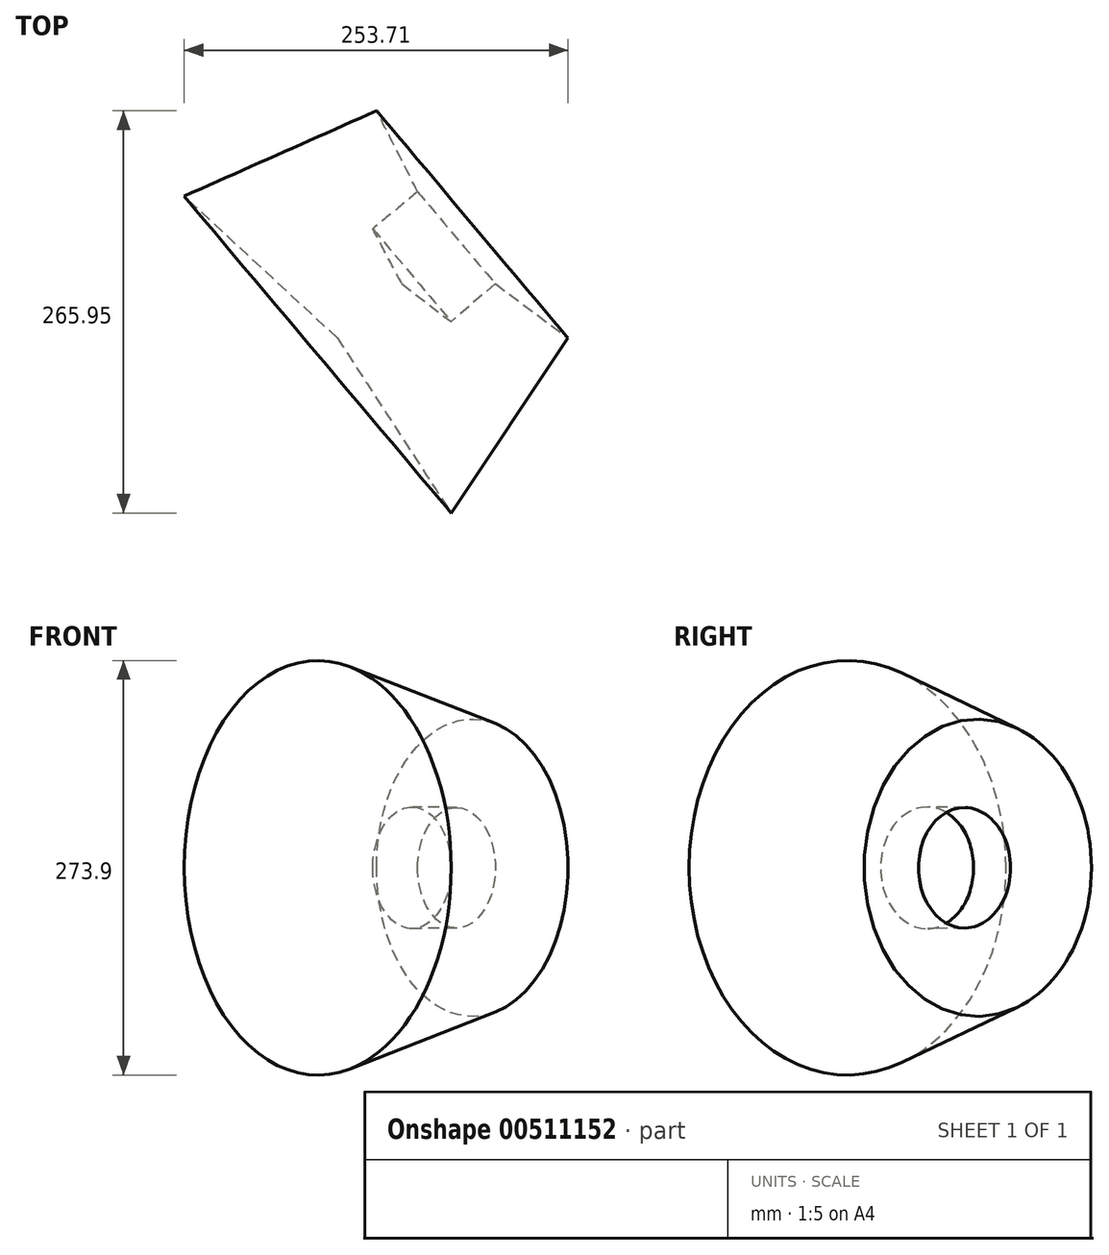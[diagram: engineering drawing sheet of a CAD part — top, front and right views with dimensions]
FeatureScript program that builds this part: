
annotation { "Feature Type Name" : "Feature", "Feature Type Description" : "" }
export const myFeature = defineFeature(function(context is Context, id is Id, definition is map)
    precondition{}
    {
        {
            var Q0;
            Q0=qCreatedBy(makeId("Top.planeOp"),FACE);
            var sketch = newSketch(context, id + "F0", { "sketchPlane" : qUnion([Q0])});
            skLineSegment(sketch, "E0", {"start": v(0, 50.57) * mm, "end": v(-32.65, 75.64) * mm});
            skLineSegment(sketch, "E1", {"start": v(-32.65, 75.64) * mm, "end": v(-75.2, 39.79) * mm});
            skLineSegment(sketch, "E2", {"start": v(-75.2, 39.79) * mm, "end": v(0, -75.93) * mm});
            skLineSegment(sketch, "E3", {"start": v(0, -75.93) * mm, "end": v(77.24, 39.79) * mm});
            skLineSegment(sketch, "E4", {"start": v(77.24, 39.79) * mm, "end": v(29.15, 75.64) * mm});
            skLineSegment(sketch, "E5", {"start": v(29.15, 75.64) * mm, "end": v(0, 50.57) * mm});
            skSolve(sketch);
        }
        {
            var Q0;
            Q0=makeQuery(id+"F0.imprint","IMPRINT",FACE,{"disambiguationData":[TD([[makeQuery(id+"F0.imprint","IMPRINT",EDGE,{"derivedFrom":sQuery(id+"F0.wireOp",EDGE,"E0")}),1.0]])]});
            var Q1;
            Q1=sQuery(id+"F0.wireOp",EDGE,"E1");
            revolve(context, id + "F1", {"entities" : qUnion([Q0]), "axis" : qUnion([Q1]), "revolveType" : RevolveType.FULL});
        }
    });
